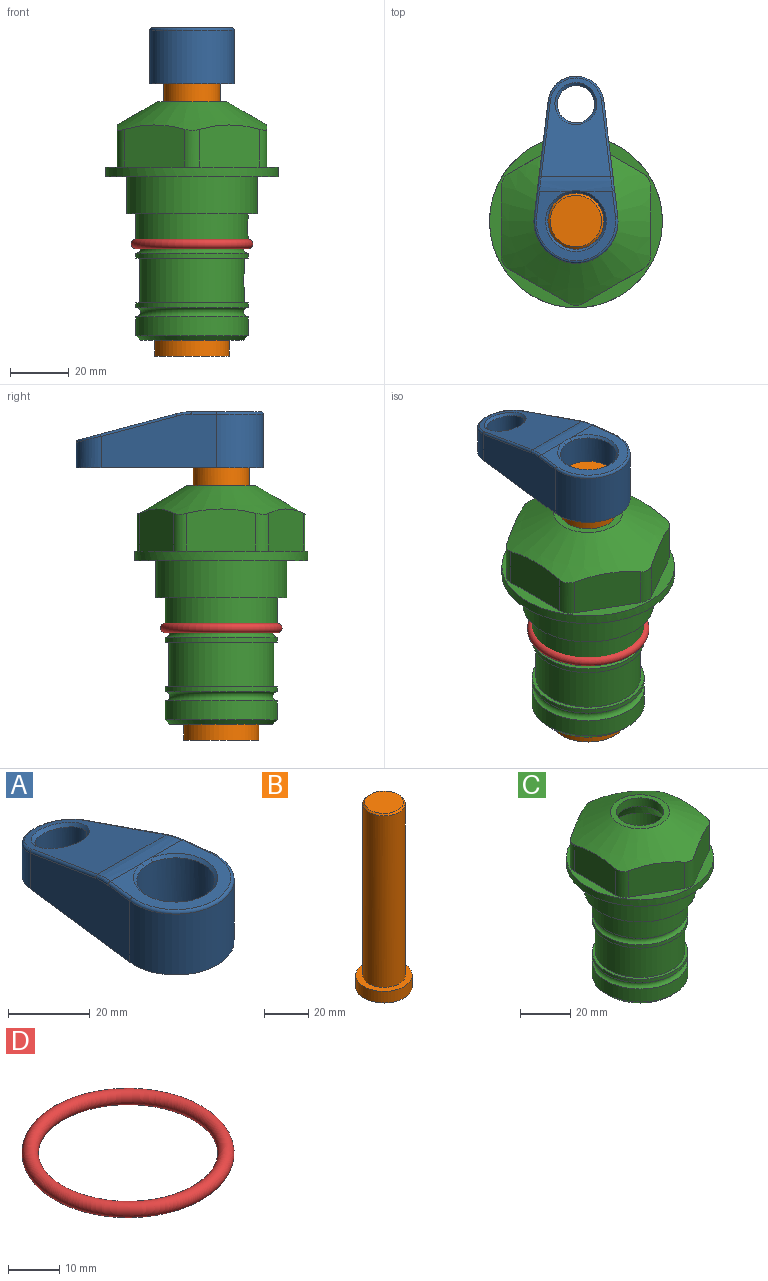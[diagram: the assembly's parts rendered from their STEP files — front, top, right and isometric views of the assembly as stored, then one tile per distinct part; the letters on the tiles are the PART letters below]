
ASSEMBLY  parts=4 mates=2
PART A: 31 faces, bbox 31.7x65.5x19.8 mm
  f0: plane 39.12x18.26mm, normal (0.99,0.12,0), area 612.2mm2, adj f1,f4,f7,f11,f13,f15
  f1: cylinder r=9.53mm len=18.91mm, axis (0,0,-1), area 296.1mm2, adj f0,f2,f7,f17
  f2: plane 39.12x18.26mm, normal (-0.99,0.12,0), area 612.2mm2, adj f1,f4,f7,f12,f14,f16
  f3: cylinder r=6.35mm len=12.7mm, axis (0,0,-1), area 362.4mm2, adj f7,f18
  f4: cylinder r=14.29mm len=28.58mm, axis (0,0,-1), area 882.2mm2, adj f0,f2,f7,f10
  f5: cylinder r=9.53mm len=19.05mm, axis (0,0,-1), area 1092.6mm2, adj f7,f19,f20
  f6: plane 26.99x23.69mm, normal (0,0,1), area 216.2mm2, adj f9,f10,f11,f12,f19
  f7: plane 63.5x28.58mm, normal (0,0,-1), area 661.8mm2, adj f0,f1,f2,f3,f4,f5,f22,f23
  f8: plane 33.52x23.6mm, normal (0,0.26,0.97), area 486mm2, adj f9,f15,f16,f17,f18
  f9: cylinder r=19.05mm len=24.72mm, axis (1,0,0), area 120.4mm2, adj f6,f8,f13,f14,f20
  f10: torus R=13.49mm, axis (0,0,1), area 59mm2, adj f4,f6,f11,f12
  f11: cylinder r=0.79mm len=8.67mm, axis (0.12,-0.99,0), area 10.8mm2, adj f0,f6,f10,f13
  f12: cylinder r=0.79mm len=8.67mm, axis (0.12,0.99,0), area 10.8mm2, adj f2,f6,f10,f14
  f13: bspline ~4.95x1.42mm, area 6.1mm2, adj f0,f9,f11,f15
  f14: bspline ~4.95x1.42mm, area 6.1mm2, adj f2,f9,f12,f16
  f15: cylinder r=0.79mm len=25.95mm, axis (0.12,-0.96,0.26), area 32.9mm2, adj f0,f8,f13,f17
  f16: cylinder r=0.79mm len=25.95mm, axis (0.12,0.96,-0.26), area 32.9mm2, adj f2,f8,f14,f17
  f17: bspline ~18.91x8.38mm, area 30mm2, adj f1,f8,f15,f16
  f18: bspline ~14.29x14.29mm, area 48.3mm2, adj f3,f8
  f19: cone r=9.53mm half-angle=45deg, axis (0,0,1), area 66.5mm2, adj f5,f6,f20
  f20: bspline ~3.22x0.96mm, area 3.5mm2, adj f5,f9,f19
  f21: plane 2.75x2.72mm, normal (0,0,-1), area 2.9mm2, adj f23,f25,f28
  f22: plane 23.05x15.88mm, normal (-0.99,-0.12,0), area 323.6mm2, adj f7,f25,f26,f27,f28,f29
  f23: plane 23.05x15.88mm, normal (0.99,-0.12,0), area 323.6mm2, adj f7,f21,f25,f27,f28,f30
  f24: cylinder r=9.53mm len=10.69mm, axis (0,0,-1), area 114.7mm2, adj f7,f27,f29,f30
  f25: cylinder r=12.7mm len=20.59mm, axis (0,0,-1), area 381.1mm2, adj f7,f21,f22,f23,f26,f28
  f26: plane 2.75x2.72mm, normal (0,0,-1), area 2.9mm2, adj f22,f25,f28
  f27: plane 19.72x18.37mm, normal (0,-0.26,-0.97), area 291.8mm2, adj f22,f23,f24,f28,f29,f30
  f28: cylinder r=15.88mm len=19.92mm, axis (1,0,0), area 54.8mm2, adj f21,f22,f23,f25,f26,f27
  f29: cylinder r=1.59mm len=11mm, axis (0,0,-1), area 34.7mm2, adj f7,f22,f24,f27
  f30: cylinder r=1.59mm len=11mm, axis (0,0,-1), area 34.7mm2, adj f7,f23,f24,f27
PART B: 6 faces, bbox 25.4x25.4x101.6 mm
  f0: plane 17.46x17.46mm, normal (0,0,1), area 239.5mm2, adj f5
  f1: plane 25.4x25.4mm, normal (0,0,-1), area 506.7mm2, adj f2
  f2: cylinder r=12.7mm len=25.4mm, axis (0,0,1), area 506.7mm2, adj f1,f3
  f3: plane 25.4x25.4mm, normal (0,0,1), area 221.7mm2, adj f2,f4
  f4: cylinder r=9.53mm len=94.46mm, axis (0,0,1), area 5653mm2, adj f3,f5
  f5: cone r=8.73mm half-angle=45deg, axis (0,0,-1), area 64.4mm2, adj f0,f4
PART C: 36 faces, bbox 58.7x58.7x81 mm
  f0: cylinder r=17.78mm len=35.56mm, axis (0,0,1), area 1670.8mm2, adj f23,f24,f31
  f1: cylinder r=19.05mm len=38.1mm, axis (0,0,1), area 1191.9mm2, adj f26,f27,f30
  f2: plane 58.66x58.66mm, normal (0,0,-1), area 1150.6mm2, adj f3,f28
  f3: cylinder r=29.33mm len=58.66mm, axis (0,0,-1), area 585.1mm2, adj f2,f4
  f4: plane 58.66x58.66mm, normal (0,0,1), area 475.9mm2, adj f3,f5,f6,f7,f8,f9,f10,f11
  f5: plane 20.32x14.34mm, normal (-0.5,0.87,0), area 324.4mm2, adj f4,f15,f16,f17
  f6: plane 20.32x14.34mm, normal (0.5,0.87,0), area 324.4mm2, adj f4,f14,f15,f17
  f7: plane 23.48x14.34mm, normal (1,0,0), area 324.4mm2, adj f4,f13,f14,f17
  f8: plane 20.32x14.34mm, normal (0.5,-0.87,0), area 324.4mm2, adj f4,f12,f13,f17
  f9: plane 20.32x14.34mm, normal (-0.5,-0.87,0), area 324.4mm2, adj f4,f11,f12,f17
  f10: plane 23.48x14.34mm, normal (-1,0,0), area 324.4mm2, adj f4,f11,f16,f17
  f11: cylinder r=5.08mm len=12.85mm, axis (0,0,-1), area 67.2mm2, adj f4,f9,f10,f17
  f12: cylinder r=5.08mm len=12.85mm, axis (0,0,-1), area 67.2mm2, adj f4,f8,f9,f17
  f13: cylinder r=5.08mm len=12.85mm, axis (0,0,-1), area 67.2mm2, adj f4,f7,f8,f17
  f14: cylinder r=5.08mm len=12.85mm, axis (0,0,-1), area 67.2mm2, adj f4,f6,f7,f17
  f15: cylinder r=5.08mm len=12.85mm, axis (0,0,-1), area 67.2mm2, adj f4,f5,f6,f17
  f16: cylinder r=5.08mm len=12.85mm, axis (0,0,-1), area 67.2mm2, adj f4,f5,f10,f17
  f17: cone r=11.73mm half-angle=60deg, axis (0,0,-1), area 2071.8mm2, adj f5,f6,f7,f8,f9,f10,f11,f12
  f18: plane 23.46x23.46mm, normal (0,0,1), area 147.4mm2, adj f17,f35
  f19: plane 34.93x34.93mm, normal (0,0,-1), area 958mm2, adj f29
  f20: cylinder r=19.05mm len=38.1mm, axis (0,0,1), area 760.1mm2, adj f21,f29
  f21: torus R=19.05mm, axis (0,0,1), area 565.3mm2, adj f20,f22
  f22: cylinder r=19.05mm len=38.1mm, axis (0,0,1), area 190mm2, adj f21,f23
  f23: plane 38.1x38.1mm, normal (0,0,1), area 146.9mm2, adj f0,f22
  f24: plane 38.1x38.1mm, normal (0,0,-1), area 146.9mm2, adj f0,f25
  f25: cylinder r=19.05mm len=38.1mm, axis (0,0,1), area 190mm2, adj f24,f26
  f26: torus R=19.05mm, axis (0,0,1), area 565.3mm2, adj f1,f25
  f27: plane 44.45x44.45mm, normal (0,0,-1), area 411.7mm2, adj f1,f28
  f28: cylinder r=22.23mm len=44.45mm, axis (0,0,1), area 1773.5mm2, adj f2,f27
  f29: cone r=19.05mm half-angle=45deg, axis (0,0,1), area 257.5mm2, adj f19,f20
  f30: cylinder r=3.17mm len=6.75mm, axis (-1,0,0), area 128mm2, adj f1,f33
  f31: cylinder r=3.17mm len=6.35mm, axis (-1,0,0), area 102.5mm2, adj f0,f33
  f32: plane 25.4x25.4mm, normal (0,0,1), area 506.7mm2, adj f33
  f33: cylinder r=12.7mm len=66.42mm, axis (0,0,-1), area 5236.2mm2, adj f30,f31,f32,f34
  f34: cone r=9.53mm half-angle=30deg, axis (0,0,-1), area 443.4mm2, adj f33,f35
  f35: cylinder r=9.53mm len=19.05mm, axis (0,0,-1), area 240.9mm2, adj f18,f34
PART D: 1 faces, bbox 44.7x44.7x3.2 mm
  f0: torus R=19.05mm, axis (0,0,1), area 1193.9mm2
PLACE A t=(0,0,9.92)mm
PLACE B at identity
PLACE C t=(0,0,22.92)mm
PLACE D t=(0,0,24.51)mm
MATE revolute B.f2 <-> A.f4  axis (0,0,1) through (0,0,63.5)mm
MATE fastened D.f0 <-> C.f0  axis (0,0,1) through (0,0,0)mm
